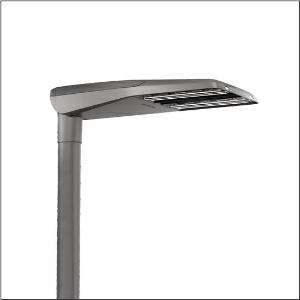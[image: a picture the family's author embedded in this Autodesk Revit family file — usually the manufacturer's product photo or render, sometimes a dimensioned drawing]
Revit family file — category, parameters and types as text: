
# Revit family: streetlight_sl_11_iq_midi___st1_0ab_5xc3n41f08le_a448
name_source: partatom
category: Lighting Fixtures
units: mm (PartAtom-declared; Revit-internal decimal feet)

## family parameters
Cut with Voids When Loaded = No
Host = Face
Light Source = No
Part Type = Normal
Room Calculation Point = No
Round Connector Dimension = Use Diameter
Shared = No

## types (1)
- --- (1 x LED, 8080 lm, 60.4 W, 4000K)
    Apparent Load = 60 VA
    CIE Flux Codes = 29 63 95 100 100
    Color Rendering = 70
    Color Temperature = 4000K
    Default Elevation = 1800 mm
    Description = Streetlight SL 11 iQ midi, mast luminaire, primary light control with 3 zone facetted reflector, of plastic, silver coated, highly specular, primary optical cover: cover, of PMMA, transparent, light distribution: ST1.0aB, light emission: direct distribution, primary light characteristic: asymmetric, installation type: post-top, side-entry, LED, High Power LED, rated luminous flux: 8.080lm, luminous efficacy: 134lm/W, light colour: 740, colour temperature: 4000K, control: optimised constant luminous flux control (CLO 2.0), Street-Remote, Desk-Remote (wireless, voltage-free reading and setting of iQ features in the workshop via application-optimized NFC function/RFID function), Light-Fading, Smart-Wire, Night-Set, Lumen-Switch, Temp-Guard, Auto-Match, with cable H07RN-F 5x 1.5mm², mains connection: 230..240V, AC, 50/60Hz, connection cable pre-assembled, cable length: 8,5m, start of lifetime: 60W, end of service life: 63W, reduction: 30W, luminaire housing, of diecast aluminium, powder-coated, Siteco® metallic grey (DB 702S), please order mast flange separately, inclination adjustable without tools: 0°, 5°, 10°, 15° (post-top) | 0°, -5°, -10°, -15° (side-entry), sealing non-destructively replaceable, multi-level sealing system, length: 780mm, width: 376mm, height: 118mm, mast flange for spigot size: 42mm (side-entry): 5XC10008XM4, 60/48mm (side-entry/post-top): 5XC10108XM2, 76/60mm (side-entry/post-top): 5XC10108XM1, equipment: standard, protection rating (complete): IP66, insulation class (complete): insulation class II (safety insulation), certification: CE, ENEC, VDE, impact resistance: IK09, permissible operating ambient temperature for outdoor applications: -25..+50°C, standard-compliant lighting for roads and squares, Environmental Product Declaration (EPD) tested and certified by an independent institute, packaging unit: 1 piece

Light Distribution: ST1.0aB
    Height = 118 mm
    Lamp = 1 x LED
    Lamp Light Flux = 8080 lm
    Lamp Power = 60.4 W
    Lamp count = 1
    Length = 780 mm
    Luminous efficacy = 134 lm/W
    Manufacturer = Siteco
    ModVariant = No
    Model = 5XC3N41F08LE
    Number of Poles = 1
    OnlyDefault = Yes
    Power Factor = 1
    Product Name = Streetlight SL 11 iQ midi | ST1.0aB
    Product group = mast luminaire | pylon top
    ProductGroupID = 6100
    Protection Class = Protection class II
    Protection Degree = IP 66
    RLX_Detail_Level = 1
    RLX_Emergency_Light_Flux = 0 lm
    RLX_Emergency_Type = 0
    RLX_Emergency_Type_DB = No
    RlxData = <blob elided: 70109 chars, md5=8aef0559>
    Socket = socket
    Standby Power = 0 W
    System Light Flux = 8080 lm
    System Power = 60 W
    Type Comments = factory setting: luminous flux: 100 % | dim-lin: 254 | 520 mA
    Type Image = l_1005960.jpg
    URL = http://relux.com
    VarID = @adj_038937
    Voltage = 0 V
    Weight = 0.00 kg
    Width = 376 mm

## geometry (parser evidence)
native form markers: Blend x4, Sweep x11
no freeform markers — native parametric forms only
